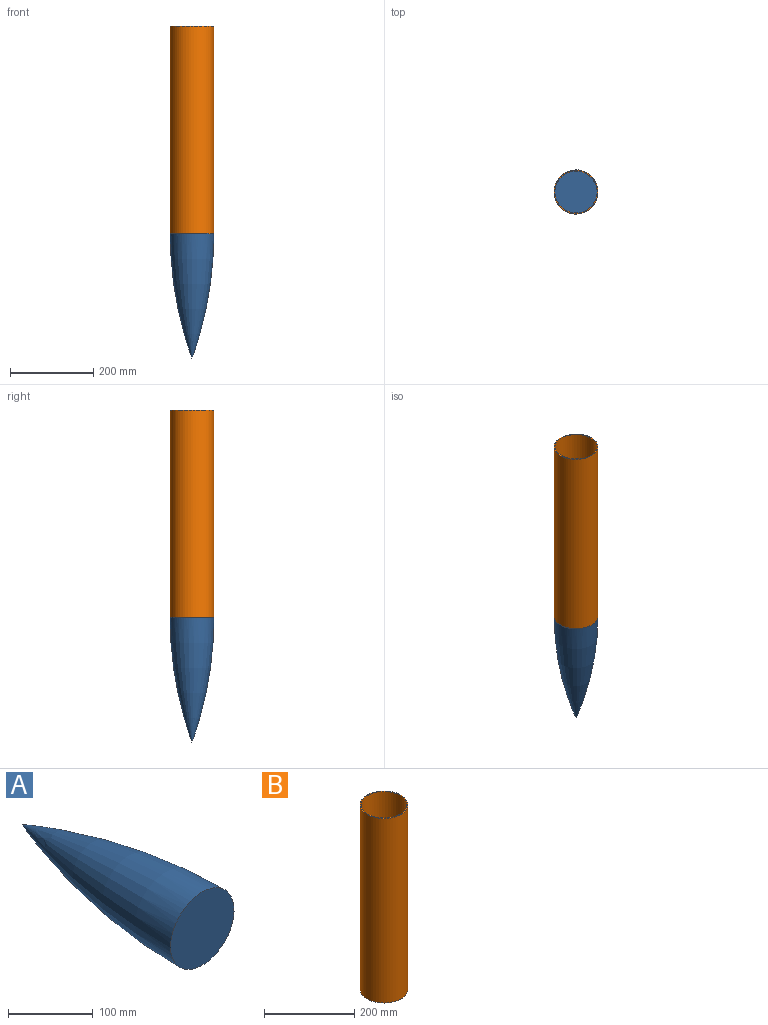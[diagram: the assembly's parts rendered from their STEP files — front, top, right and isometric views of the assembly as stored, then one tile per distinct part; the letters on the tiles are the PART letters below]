
ASSEMBLY  parts=2 mates=1
PART A: 2 faces, bbox 105.6x0x105.6 mm
  f0: plane 105.6x105.6mm, normal (0,-1,0), area 8758.3mm2, adj f1
  f1: revolved ~105.6x105.6mm, area 0mm2, adj f0
PART B: 4 faces, bbox 105.6x105.6x500 mm
  f0: cylinder r=50.8mm len=500mm, axis (0,0,-1), area 159592.9mm2, adj f2,f3
  f1: cylinder r=52.8mm len=500mm, axis (0,0,-1), area 165876.1mm2, adj f2,f3
  f2: plane 105.6x105.6mm, normal (0,0,1), area 650.9mm2, adj f0,f1
  f3: plane 105.6x105.6mm, normal (0,0,-1), area 650.9mm2, adj f0,f1
PLACE A rot(axis=(-0.99,0.09,-0.09),90.4deg) t=(0,0,0)mm
PLACE B at identity
MATE cylindrical B.f0 <-> A.f0  axis (0,0,1) through (0,0,500)mm
